# Revit family: NAU_Naughtone_Stng_Hue_Sofa
name_source: partatom
category: Furniture
revit_build: Autodesk Revit 2018 (Build: 20170223_1515(x64)
units: mm (PartAtom-declared; Revit-internal decimal feet)

## family parameters
Always vertical = Yes
Cut with Voids When Loaded = No
OmniClass Number = 23.40.20.00
OmniClass Title = General Furniture and Specialties
Room Calculation Point = No
Shared = Yes
Work Plane-Based = No

## types (2) — shared parameters
Assembly Code = E2020200
AssetType = Movable
BIMObjectName = NAU_Naughtone_Seating_Hue_Sofa
Category = Pr_40_50_12 : Chairs, seats and benches
Color = Various
DurationUnit = year
Finish = Fabric upholstery
IfcExportAs = IfcFurnishingElementType
IfcExportType = SOFA
Keynote = Pr_40_50_12
MainColor = Various
ManufacturerAddress = Knaresborough Tech Park, Manse Lane, Knaresborough, HG5 8LF
ManufacturerName = Naughtone
ManufacturerURL = www.naughtone.com/
Material = Legs in 16 RAL Colours
NBSDescription = Seating
NBSReference = 45-35-72/352
Name = Seating_Hue_Sofa_Naughtone
NominalLength = 1400 mm  [stored 4.59318 ft]
NominalWidth = 630 mm  [stored 2.06693 ft]
ProductInformation = www.naughtone.com/products/hue/
Shape = Rectangular
SustainabilityPerformance = FSC certifeied, SCS indoor advantage gold
URL = www.naughtone.com
Uniclass2015Code = Pr_40_50_12
Uniclass2015Title = Chairs, seats and benches
Version = 1
WarrantyDescription = Request warranty information from naughtone
WarrantyDurationLabor = 7
WarrantyDurationParts = 7
WarrantyDurationUnit = year

## per-type parameters (varying)
| type | Description | HighestSeatingHeight | IsBarHeight | LowestSeatingHeight | Model | ModelNumber | ModelReference | NominalHeight | SeatingHeight | Size |
| HUE2NAST - Hue Sofa with Steel Legs | Hue Sofa with Steel Legs | 450 mm  [stored 1.47638 ft] | No | 450 mm  [stored 1.47638 ft] | HUE2NAST | HUE2NAST | Hue Sofa with Steel Legs | 750 mm  [stored 2.46063 ft] | 450 mm  [stored 1.47638 ft] | 1400 x 630 x 750mm |
| HUEBH2NAST - Hue Bar Height Sofa with Steel Legs | Hue Bar Height Sofa with Steel Legs | 750 mm  [stored 2.46063 ft] | Yes | 750 mm  [stored 2.46063 ft] | HUEBH2NAST | HUEBH2NAST | Hue Bar Height Sofa with Steel Legs | 1050 mm | 750 mm  [stored 2.46063 ft] | 1400 x 630 x 1050mm |

note: [stored X ft] marks values corroborated as IEEE doubles in the binary element streams (Revit-internal decimal feet)

## geometry (parser evidence)
native form markers: Sweep x4
no freeform markers — native parametric forms only
